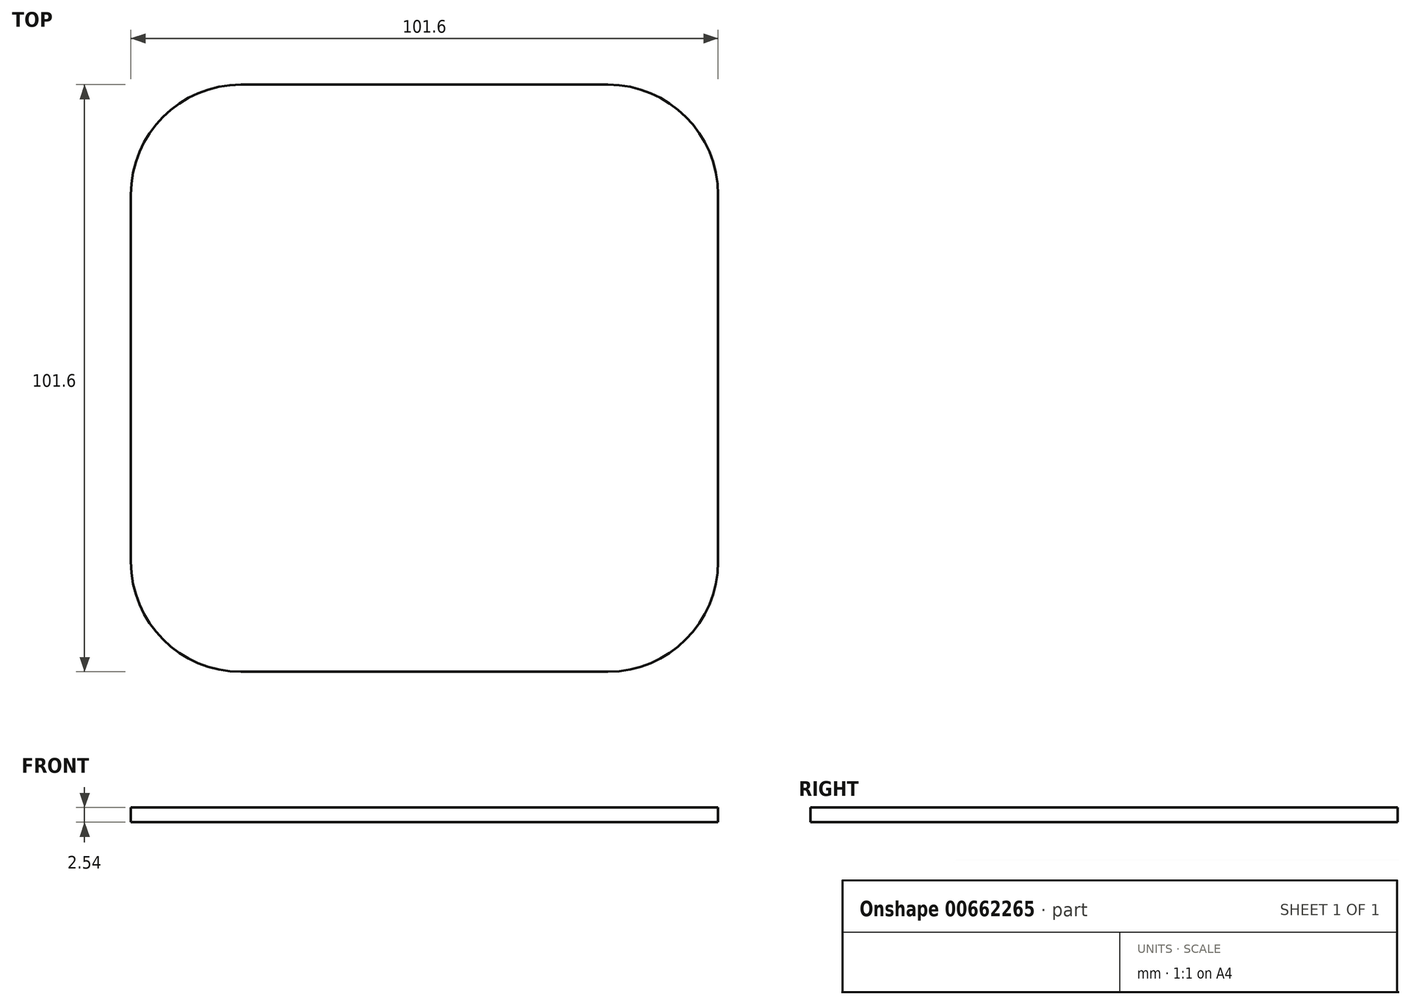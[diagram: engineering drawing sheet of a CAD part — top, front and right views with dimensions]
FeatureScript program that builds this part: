
annotation { "Feature Type Name" : "Feature", "Feature Type Description" : "" }
export const myFeature = defineFeature(function(context is Context, id is Id, definition is map)
    precondition{}
    {
        {
            var Q0;
            Q0=qCreatedBy(makeId("Top.planeOp"),FACE);
            var sketch = newSketch(context, id + "F0", { "sketchPlane" : qUnion([Q0])});
            skPoint(sketch, "E0.middle", {"position": v(0, 0) * mm});
            skLineSegment(sketch, "E1.bottom", {"start": v(31.75, -50.8) * mm, "end": v(-31.75, -50.8) * mm});
            skLineSegment(sketch, "E1.top", {"start": v(31.75, 50.8) * mm, "end": v(-31.75, 50.8) * mm});
            skLineSegment(sketch, "E1.left", {"start": v(50.8, -31.75) * mm, "end": v(50.8, 31.75) * mm});
            skLineSegment(sketch, "E1.right", {"start": v(-50.8, -31.75) * mm, "end": v(-50.8, 31.75) * mm});
            skPoint(sketch, "E2.visualSharp", {"position": v(-50.8, 50.8) * mm});
            skArc(sketch, "E2.filletArc", {"start": v(-31.75, 50.8) * mm, "mid": v(-45.22, 45.22) * mm, "end": v(-50.8, 31.75) * mm});
            skPoint(sketch, "E3.visualSharp", {"position": v(-50.8, -50.8) * mm});
            skArc(sketch, "E3.filletArc", {"start": v(-50.8, -31.75) * mm, "mid": v(-45.22, -45.22) * mm, "end": v(-31.75, -50.8) * mm});
            skArc(sketch, "E4.filletArc", {"start": v(31.75, -50.8) * mm, "mid": v(45.22, -45.22) * mm, "end": v(50.8, -31.75) * mm});
            skArc(sketch, "E5.filletArc", {"start": v(50.8, 31.75) * mm, "mid": v(45.22, 45.22) * mm, "end": v(31.75, 50.8) * mm});
            skSolve(sketch);
        }
        {
            var Q0;
            Q0=qSketchRegion(id+"F0",true);
            extrude(context, id + "F1", {"entities" : qUnion([Q0]), "depth" : 2.54 * mm, "offsetDistance" : 25.4 * mm});
        }
    });
